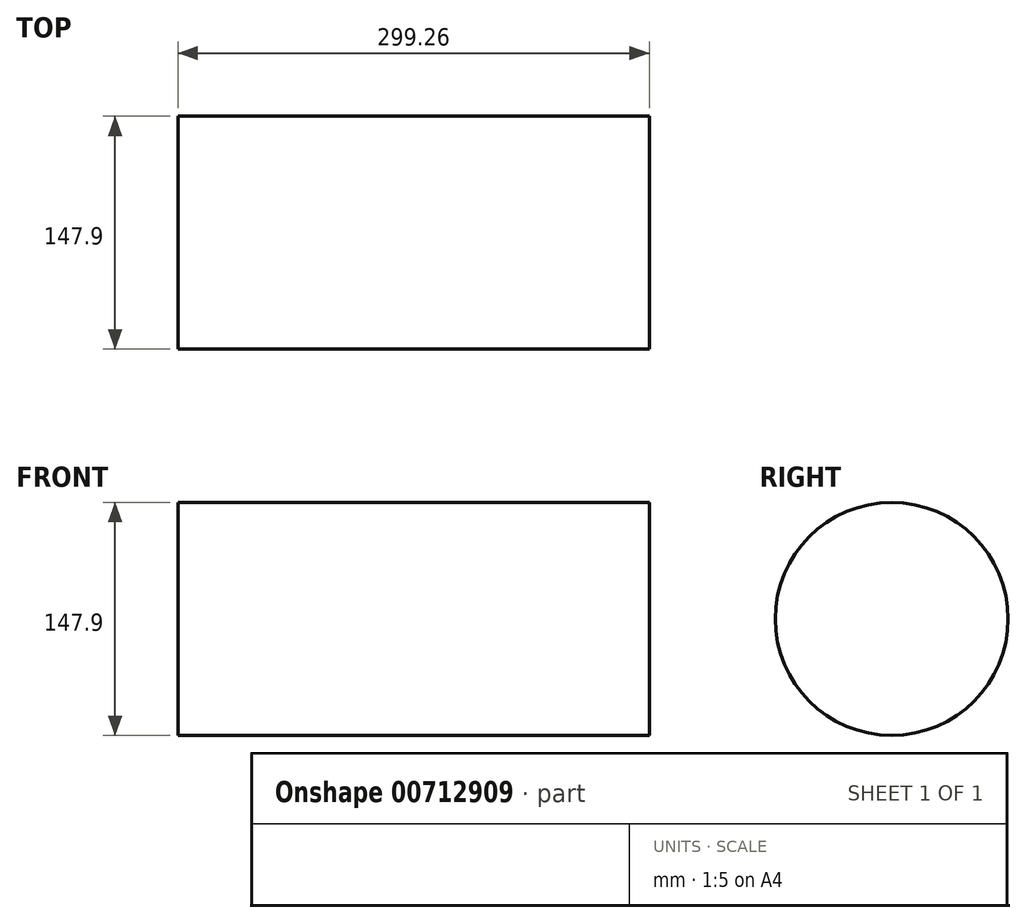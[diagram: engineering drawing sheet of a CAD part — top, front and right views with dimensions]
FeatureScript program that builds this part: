
annotation { "Feature Type Name" : "Feature", "Feature Type Description" : "" }
export const myFeature = defineFeature(function(context is Context, id is Id, definition is map)
    precondition{}
    {
        {
            var Q0;
            Q0=qCreatedBy(makeId("Right.planeOp"),FACE);
            var sketch = newSketch(context, id + "F0", { "sketchPlane" : qUnion([Q0])});
            skCircle(sketch, "E0", {"center": v(0, 0) * mm, "radius": 73.95 * mm});
            skSolve(sketch);
        }
        {
            var Q0;
            Q0=sQuery(id+"F0.wireOp",EDGE,"E0");
            extrude(context, id + "F1", {"bodyType" : ToolBodyType.SURFACE, "surfaceEntities" : qUnion([Q0]), "depth" : 299.26 * mm, "offsetDistance" : 25.4 * mm});
        }
    });
